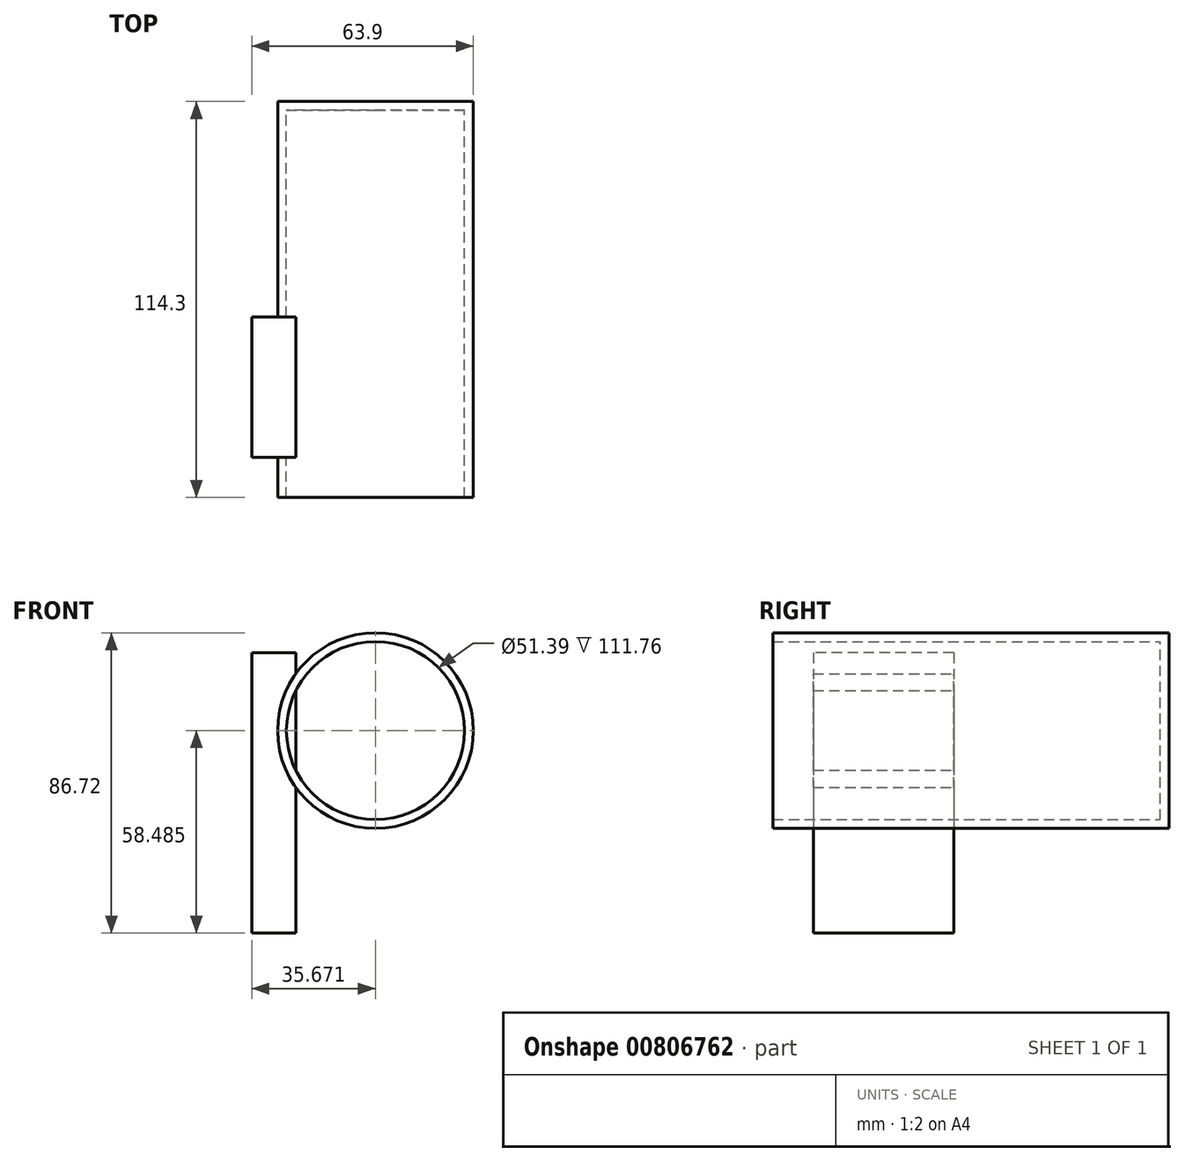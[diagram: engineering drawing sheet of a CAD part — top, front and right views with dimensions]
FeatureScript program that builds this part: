
annotation { "Feature Type Name" : "Feature", "Feature Type Description" : "" }
export const myFeature = defineFeature(function(context is Context, id is Id, definition is map)
    precondition{}
    {
        {
            var Q0;
            Q0=qCreatedBy(makeId("Front.planeOp"),FACE);
            var sketch = newSketch(context, id + "F0", { "sketchPlane" : qUnion([Q0])});
            skCircle(sketch, "E0", {"center": v(35.67, 42.3) * mm, "radius": 28.23 * mm});
            skSolve(sketch);
        }
        {
            var Q0;
            Q0=makeQuery(id+"F0.imprint","IMPRINT",FACE,{"disambiguationData":[TD([[makeQuery(id+"F0.imprint","IMPRINT",EDGE,{"derivedFrom":sQuery(id+"F0.wireOp",EDGE,"E0")}),1.0]])]});
            extrude(context, id + "F1", {"entities" : qUnion([Q0]), "depth" : 114.3 * mm, "offsetDistance" : 25.4 * mm});
        }
        {
            var Q0;
            Q0=makeQuery(id+"F1.opExtrude","CAP_FACE",FACE,{"disambiguationData":[OSD([sQuery(id+"F0.wireOp",EDGE,"E0")])],"isStart":false});
            shell(context, id + "F2", {"entities" : qUnion([Q0]), "thickness" : 2.54 * mm});
        }
        {
            var Q0;
            Q0=qCreatedBy(makeId("Right.planeOp"),FACE);
            var sketch = newSketch(context, id + "F3", { "sketchPlane" : qUnion([Q0])});
            skLineSegment(sketch, "E1.bottom", {"start": v(-62.13, 64.72) * mm, "end": v(-102.63, 64.72) * mm});
            skLineSegment(sketch, "E1.top", {"start": v(-62.13, -16.18) * mm, "end": v(-102.63, -16.18) * mm});
            skLineSegment(sketch, "E1.left", {"start": v(-62.13, 64.72) * mm, "end": v(-62.13, -16.18) * mm});
            skLineSegment(sketch, "E1.right", {"start": v(-102.63, 64.72) * mm, "end": v(-102.63, -16.18) * mm});
            skSolve(sketch);
        }
        {
            var Q0;
            Q0=makeQuery(id+"F3.imprint","IMPRINT",FACE,{"disambiguationData":[TD([[makeQuery(id+"F3.imprint","IMPRINT",EDGE,{"derivedFrom":sQuery(id+"F3.wireOp",EDGE,"E1.bottom")}),1.0]])]});
            extrude(context, id + "F4", {"entities" : qUnion([Q0]), "operationType" : NewBodyOperationType.ADD, "depth" : 12.7 * mm, "offsetDistance" : 25.4 * mm});
        }
    });
